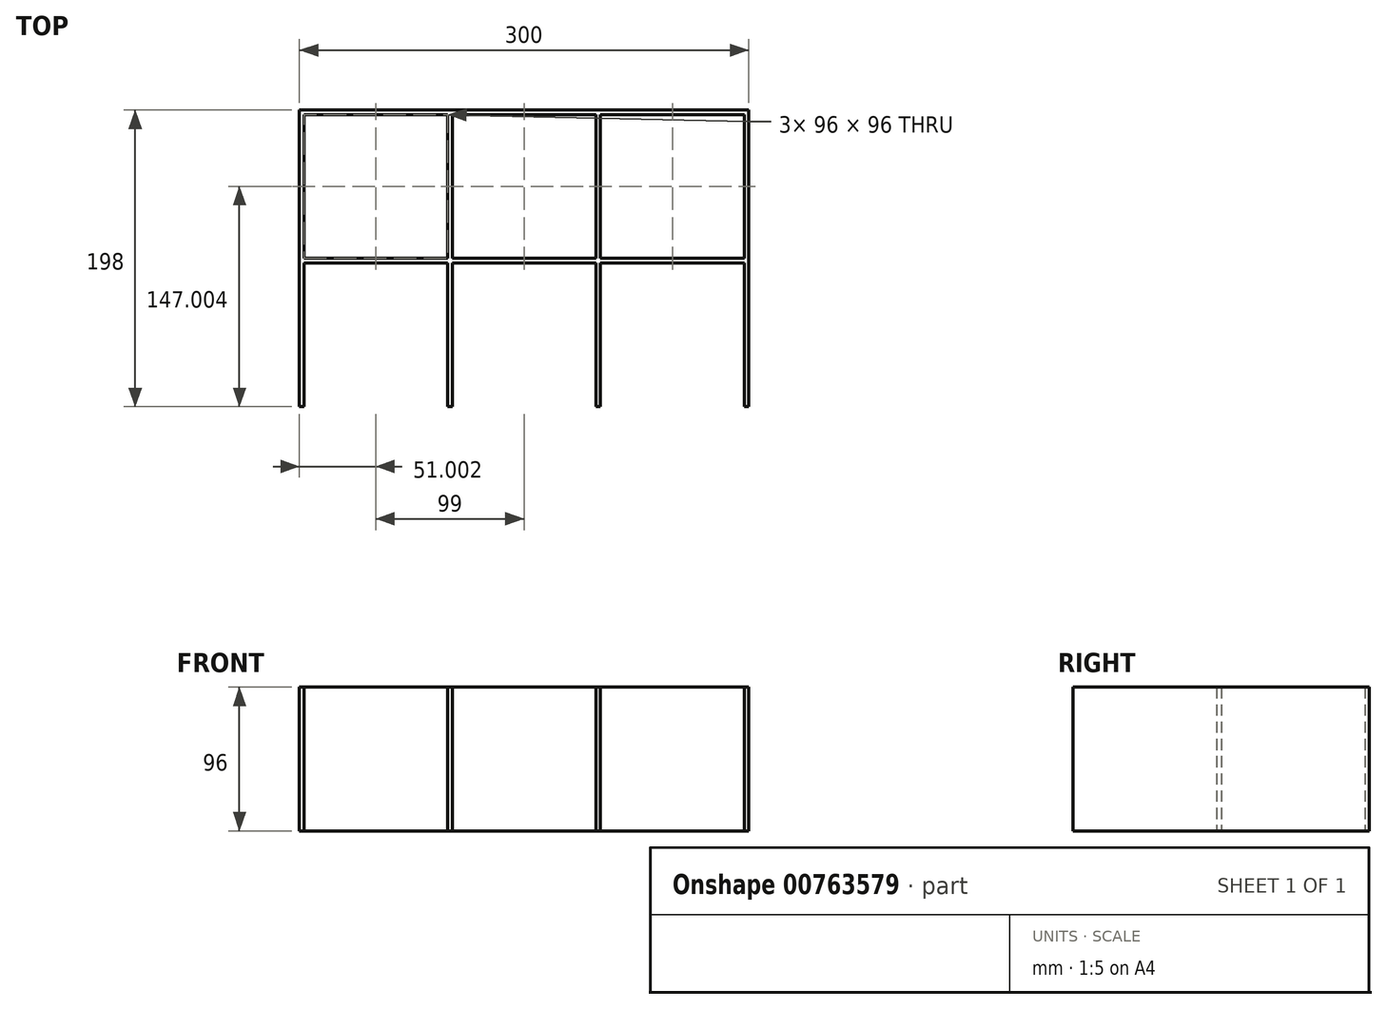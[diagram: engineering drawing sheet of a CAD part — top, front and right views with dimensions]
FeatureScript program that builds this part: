
annotation { "Feature Type Name" : "Feature", "Feature Type Description" : "" }
export const myFeature = defineFeature(function(context is Context, id is Id, definition is map)
    precondition{}
    {
        {
            assignVariable(context, id + "F0", {"name" : "popw", "anyValue" : 96});
        }
        {
            var Q0;
            Q0=qCreatedBy(makeId("Top.planeOp"),FACE);
            var sketch = newSketch(context, id + "F1", { "sketchPlane" : qUnion([Q0])});
            skLineSegment(sketch, "E0.bottom", {"start": v(-182.8, 26.13) * mm, "end": v(-86.8, 26.13) * mm});
            skLineSegment(sketch, "E0.left", {"start": v(-182.8, 26.13) * mm, "end": v(-182.8, -69.87) * mm});
            skLineSegment(sketch, "E0.right", {"start": v(-86.8, 26.13) * mm, "end": v(-86.8, -69.87) * mm});
            skLineSegment(sketch, "E1.bottom", {"start": v(-83.8, 26.13) * mm, "end": v(12.2, 26.13) * mm});
            skLineSegment(sketch, "E1.left", {"start": v(-83.8, 26.13) * mm, "end": v(-83.8, -69.87) * mm});
            skLineSegment(sketch, "E1.right", {"start": v(12.2, 26.13) * mm, "end": v(12.2, -69.87) * mm});
            skLineSegment(sketch, "E2", {"start": v(-86.8, 11.93) * mm, "end": v(-83.8, 11.93) * mm, "construction": true});
            skLineSegment(sketch, "E3.bottom", {"start": v(15.2, 26.13) * mm, "end": v(111.2, 26.13) * mm});
            skLineSegment(sketch, "E3.left", {"start": v(15.2, 26.13) * mm, "end": v(15.2, -69.87) * mm});
            skLineSegment(sketch, "E3.right", {"start": v(111.2, 26.13) * mm, "end": v(111.2, -69.87) * mm});
            skLineSegment(sketch, "E4", {"start": v(12.2, 2.63) * mm, "end": v(15.2, 2.63) * mm, "construction": true});
            skLineSegment(sketch, "E5.bottom", {"start": v(-182.8, 125.13) * mm, "end": v(-86.8, 125.13) * mm});
            skLineSegment(sketch, "E5.top", {"start": v(-182.8, 29.13) * mm, "end": v(-86.8, 29.13) * mm});
            skLineSegment(sketch, "E5.left", {"start": v(-182.8, 125.13) * mm, "end": v(-182.8, 29.13) * mm});
            skLineSegment(sketch, "E5.right", {"start": v(-86.8, 125.13) * mm, "end": v(-86.8, 29.13) * mm});
            skLineSegment(sketch, "E6.bottom", {"start": v(-83.8, 125.13) * mm, "end": v(12.2, 125.13) * mm});
            skLineSegment(sketch, "E6.top", {"start": v(-83.8, 29.13) * mm, "end": v(12.2, 29.13) * mm});
            skLineSegment(sketch, "E6.left", {"start": v(-83.8, 125.13) * mm, "end": v(-83.8, 29.13) * mm});
            skLineSegment(sketch, "E6.right", {"start": v(12.2, 125.13) * mm, "end": v(12.2, 29.13) * mm});
            skLineSegment(sketch, "E7", {"start": v(-86.8, -52.26) * mm, "end": v(-83.8, -52.26) * mm, "construction": true});
            skLineSegment(sketch, "E8.bottom", {"start": v(15.2, 125.13) * mm, "end": v(111.2, 125.13) * mm});
            skLineSegment(sketch, "E8.top", {"start": v(15.2, 29.13) * mm, "end": v(111.2, 29.13) * mm});
            skLineSegment(sketch, "E8.left", {"start": v(15.2, 125.13) * mm, "end": v(15.2, 29.13) * mm});
            skLineSegment(sketch, "E8.right", {"start": v(111.2, 125.13) * mm, "end": v(111.2, 29.13) * mm});
            skLineSegment(sketch, "E9", {"start": v(12.2, -61.57) * mm, "end": v(15.2, -61.57) * mm, "construction": true});
            skLineSegment(sketch, "E10", {"start": v(12.2, 125.13) * mm, "end": v(15.2, 125.13) * mm, "construction": true});
            skLineSegment(sketch, "E11", {"start": v(-86.8, 125.13) * mm, "end": v(-83.8, 125.13) * mm, "construction": true});
            skLineSegment(sketch, "E12", {"start": v(111.2, 26.13) * mm, "end": v(111.2, 29.13) * mm});
            skLineSegment(sketch, "E13.top", {"start": v(-182.8, 128.13) * mm, "end": v(-86.8, 128.13) * mm});
            skLineSegment(sketch, "E14.top", {"start": v(-83.8, 128.13) * mm, "end": v(12.2, 128.13) * mm});
            skLineSegment(sketch, "E15.top", {"start": v(15.2, 128.13) * mm, "end": v(111.2, 128.13) * mm});
            skLineSegment(sketch, "E16", {"start": v(-86.8, 128.13) * mm, "end": v(-83.8, 128.13) * mm});
            skLineSegment(sketch, "E17", {"start": v(12.2, 128.13) * mm, "end": v(15.2, 128.13) * mm});
            skLineSegment(sketch, "E18", {"start": v(-182.8, 128.13) * mm, "end": v(-185.8, 128.13) * mm});
            skLineSegment(sketch, "E19", {"start": v(-185.8, 128.13) * mm, "end": v(-185.8, -69.77) * mm});
            skLineSegment(sketch, "E20", {"start": v(-185.8, 128.13) * mm, "end": v(-182.8, 128.13) * mm});
            skLineSegment(sketch, "E21", {"start": v(111.2, 128.13) * mm, "end": v(114.2, 128.13) * mm});
            skLineSegment(sketch, "E22", {"start": v(114.2, 128.13) * mm, "end": v(114.2, -69.87) * mm});
            skLineSegment(sketch, "E23", {"start": v(114.2, -69.87) * mm, "end": v(111.2, -69.87) * mm});
            skLineSegment(sketch, "E24", {"start": v(-185.8, -69.77) * mm, "end": v(-182.8, -69.87) * mm});
            skLineSegment(sketch, "E25", {"start": v(-86.8, -69.87) * mm, "end": v(-83.8, -69.87) * mm});
            skLineSegment(sketch, "E26", {"start": v(12.2, -69.87) * mm, "end": v(15.2, -69.87) * mm});
            skSolve(sketch);
        }
        {
            var Q0;
            Q0=makeQuery(id+"F1.imprint","IMPRINT",FACE,{"disambiguationData":[TD([[makeQuery(id+"F1.imprint","IMPRINT",EDGE,{"derivedFrom":sQuery(id+"F1.wireOp",EDGE,"E0.bottom")}),1.0]])]});
            extrude(context, id + "F2", {"entities" : qUnion([Q0]), "depth" : (getVariable(context, 'popw')) * mm, "offsetDistance" : 25 * mm});
        }
    });
